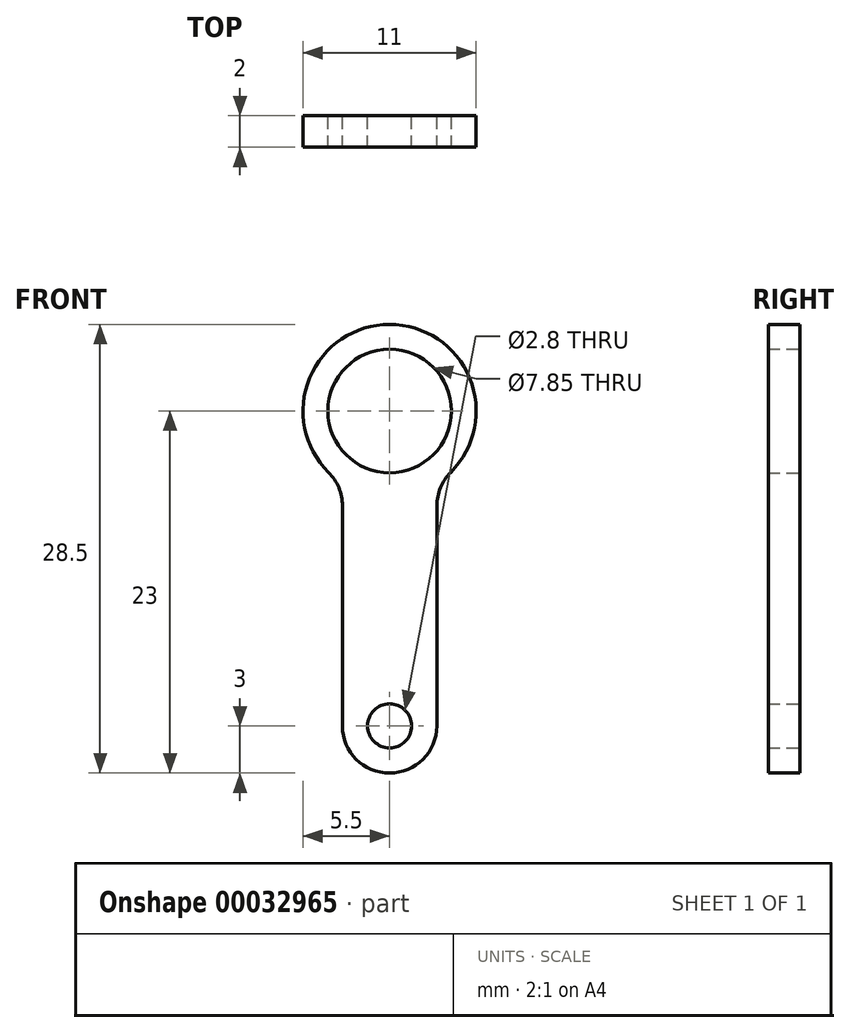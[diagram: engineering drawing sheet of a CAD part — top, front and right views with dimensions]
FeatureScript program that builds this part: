
annotation { "Feature Type Name" : "Feature", "Feature Type Description" : "" }
export const myFeature = defineFeature(function(context is Context, id is Id, definition is map)
    precondition{}
    {
        {
            var Q0;
            Q0=qCreatedBy(makeId("Front.planeOp"),FACE);
            var sketch = newSketch(context, id + "F0", { "sketchPlane" : qUnion([Q0])});
            skLineSegment(sketch, "E0", {"start": v(-3, 10) * mm, "end": v(3, 10) * mm, "construction": true});
            skLineSegment(sketch, "E1", {"start": v(-3, 3.98) * mm, "end": v(-3, 0) * mm});
            skLineSegment(sketch, "E2.MirrorCS", {"start": v(3, 3.98) * mm, "end": v(3, 0) * mm});
            skLineSegment(sketch, "E3.MirrorCS", {"start": v(3, -10) * mm, "end": v(3, 0) * mm});
            skLineSegment(sketch, "E4.MirrorCS", {"start": v(-3, -10) * mm, "end": v(-3, 0) * mm});
            skArc(sketch, "E5.MirrorCS", {"start": v(3, -10) * mm, "mid": v(0, -13) * mm, "end": v(-3, -10) * mm});
            skCircle(sketch, "E6.MirrorC", {"center": v(0, -10) * mm, "radius": 1.4 * mm});
            skCircle(sketch, "E7", {"center": v(0, 10) * mm, "radius": 3.92 * mm});
            skArc(sketch, "E8", {"start": v(3.88, 6.1) * mm, "mid": v(0, 15.5) * mm, "end": v(-3.88, 6.1) * mm});
            skPoint(sketch, "E9.orphan", {"position": v(3, 10) * mm});
            skPoint(sketch, "E10.visualSharp", {"position": v(-3, 5.4) * mm});
            skArc(sketch, "E10.filletArc", {"start": v(-3, 3.98) * mm, "mid": v(-3.23, 5.13) * mm, "end": v(-3.88, 6.1) * mm});
            skPoint(sketch, "E11.visualSharp", {"position": v(3, 5.4) * mm});
            skArc(sketch, "E11.filletArc", {"start": v(3.88, 6.1) * mm, "mid": v(3.23, 5.13) * mm, "end": v(3, 3.98) * mm});
            skSolve(sketch);
        }
        {
            var Q0;
            Q0=qSketchRegion(id+"F0",true);
            extrude(context, id + "F1", {"entities" : qUnion([Q0]), "depth" : 2 * mm});
        }
    });
